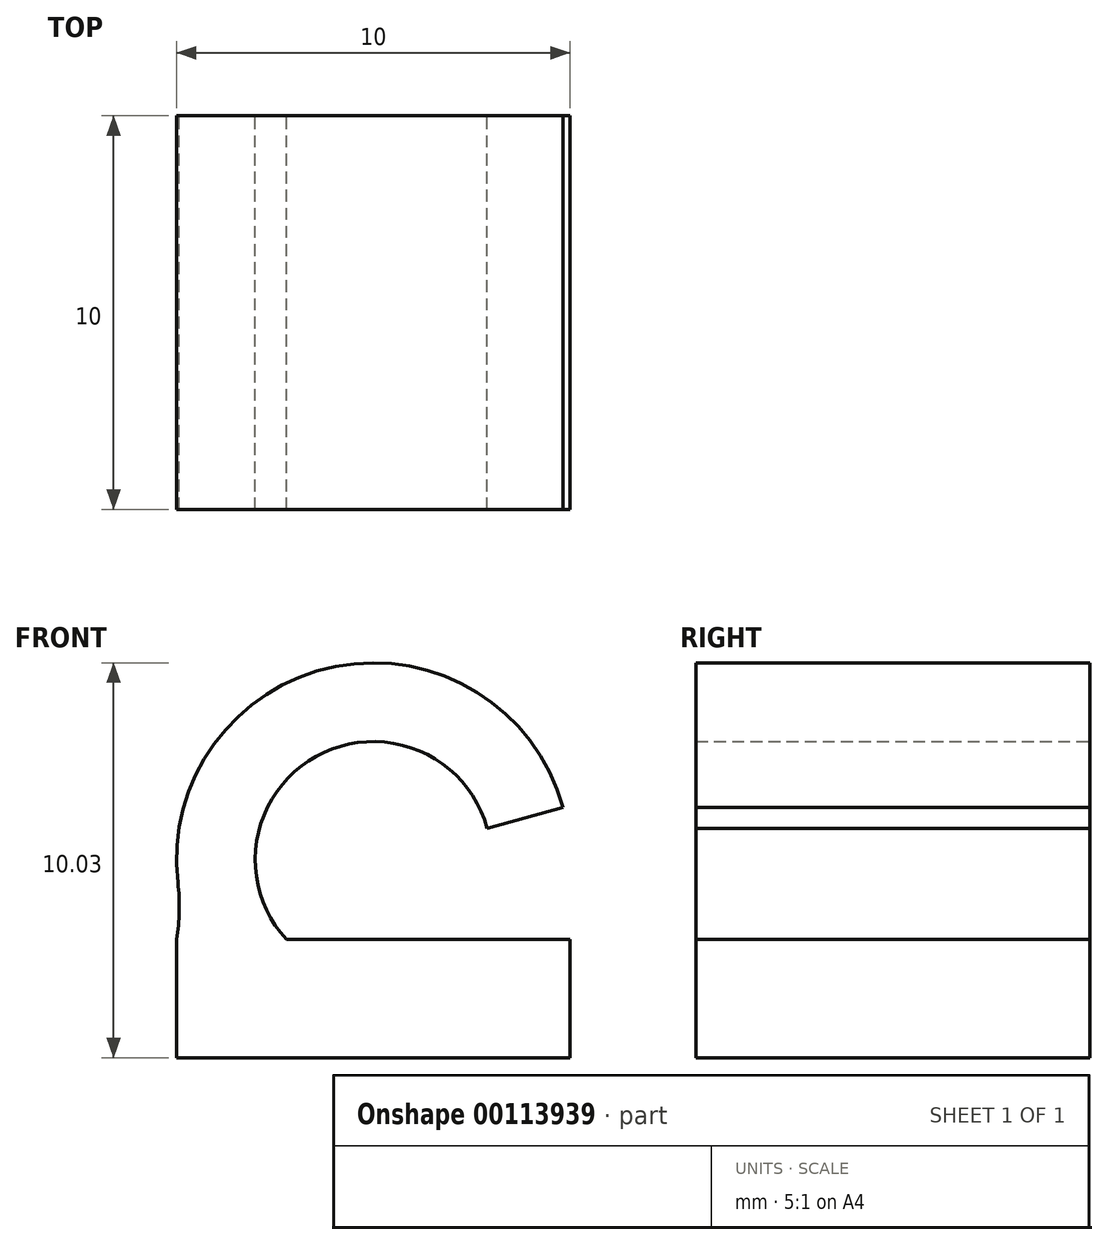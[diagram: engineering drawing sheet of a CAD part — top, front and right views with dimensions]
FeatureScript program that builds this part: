
annotation { "Feature Type Name" : "Feature", "Feature Type Description" : "" }
export const myFeature = defineFeature(function(context is Context, id is Id, definition is map)
    precondition{}
    {
        {
            var Q0;
            Q0=qCreatedBy(makeId("Top.planeOp"),FACE);
            var sketch = newSketch(context, id + "F0", { "sketchPlane" : qUnion([Q0])});
            skLineSegment(sketch, "E0.bottom", {"start": v(5, -5) * mm, "end": v(-5, -5) * mm});
            skLineSegment(sketch, "E0.top", {"start": v(5, 5) * mm, "end": v(-5, 5) * mm});
            skLineSegment(sketch, "E0.left", {"start": v(5, -5) * mm, "end": v(5, 5) * mm});
            skLineSegment(sketch, "E0.right", {"start": v(-5, -5) * mm, "end": v(-5, 5) * mm});
            skPoint(sketch, "E0.middle", {"position": v(0, 0) * mm});
            skSolve(sketch);
        }
        {
            var Q0;
            Q0=makeQuery(id+"F0.imprint","IMPRINT",FACE,{"disambiguationData":[TD([[makeQuery(id+"F0.imprint","IMPRINT",EDGE,{"derivedFrom":sQuery(id+"F0.wireOp",EDGE,"E0.bottom")}),-1.0]])]});
            extrude(context, id + "F1", {"entities" : qUnion([Q0]), "oppositeDirection" : true, "depth" : 3 * mm});
        }
        {
            var Q0;
            Q0=makeQuery(id+"F1.opExtrude","SWEPT_FACE",FACE,{"disambiguationData":[OSD([sQuery(id+"F0.wireOp",EDGE,"E0.top")])]});
            var sketch = newSketch(context, id + "F2", { "sketchPlane" : qUnion([Q0])});
            skArc(sketch, "E1", {"start": v(0, -2.97) * mm, "mid": v(3.98, 5.06) * mm, "end": v(-4.82, 3.36) * mm});
            skPoint(sketch, "E1.centerSnap0", {"position": v(0, 0) * mm});
            skArc(sketch, "E2", {"start": v(0, -0.97) * mm, "mid": v(2.39, 3.85) * mm, "end": v(-2.9, 2.83) * mm});
            skLineSegment(sketch, "E3.trimOffspring", {"start": v(-2.9, 2.83) * mm, "end": v(-4.82, 3.36) * mm});
            skLineSegment(sketch, "E4.trimOffspring", {"start": v(0, 0) * mm, "end": v(0, -2.97) * mm});
            skSolve(sketch);
        }
        {
            var Q0;
            Q0 = qSketchRegion(id + "F2", true);
            extrude(context, id + "F3", {"entities" : qUnion([Q0]), "operationType" : NewBodyOperationType.ADD, "oppositeDirection" : true, "depth" : 10 * mm});
        }
        {
            var Q0;
            Q0=makeQuery(id+"F3.boolean.opBoolean","INTERSECT",EDGE,{"derivedFrom":[makeQuery(id+"F1.opExtrude","CAP_FACE",FACE,{"disambiguationData":[OSD([sQuery(id+"F0.wireOp",EDGE,"E0.bottom"),sQuery(id+"F0.wireOp",EDGE,"E0.top"),sQuery(id+"F0.wireOp",EDGE,"E0.left"),sQuery(id+"F0.wireOp",EDGE,"E0.right")])],"isStart":true}),makeQuery(id+"F3.opExtrude","SWEPT_FACE",FACE,{"disambiguationData":[OSD([sQuery(id+"F2.wireOp",EDGE,"E1")])]})]});
            fillet(context, id + "F4", {"entities" : qUnion([Q0]), "radius" : 5 * mm, "tangentPropagation" : true, "allowEdgeOverflow" : false});
        }
    });
